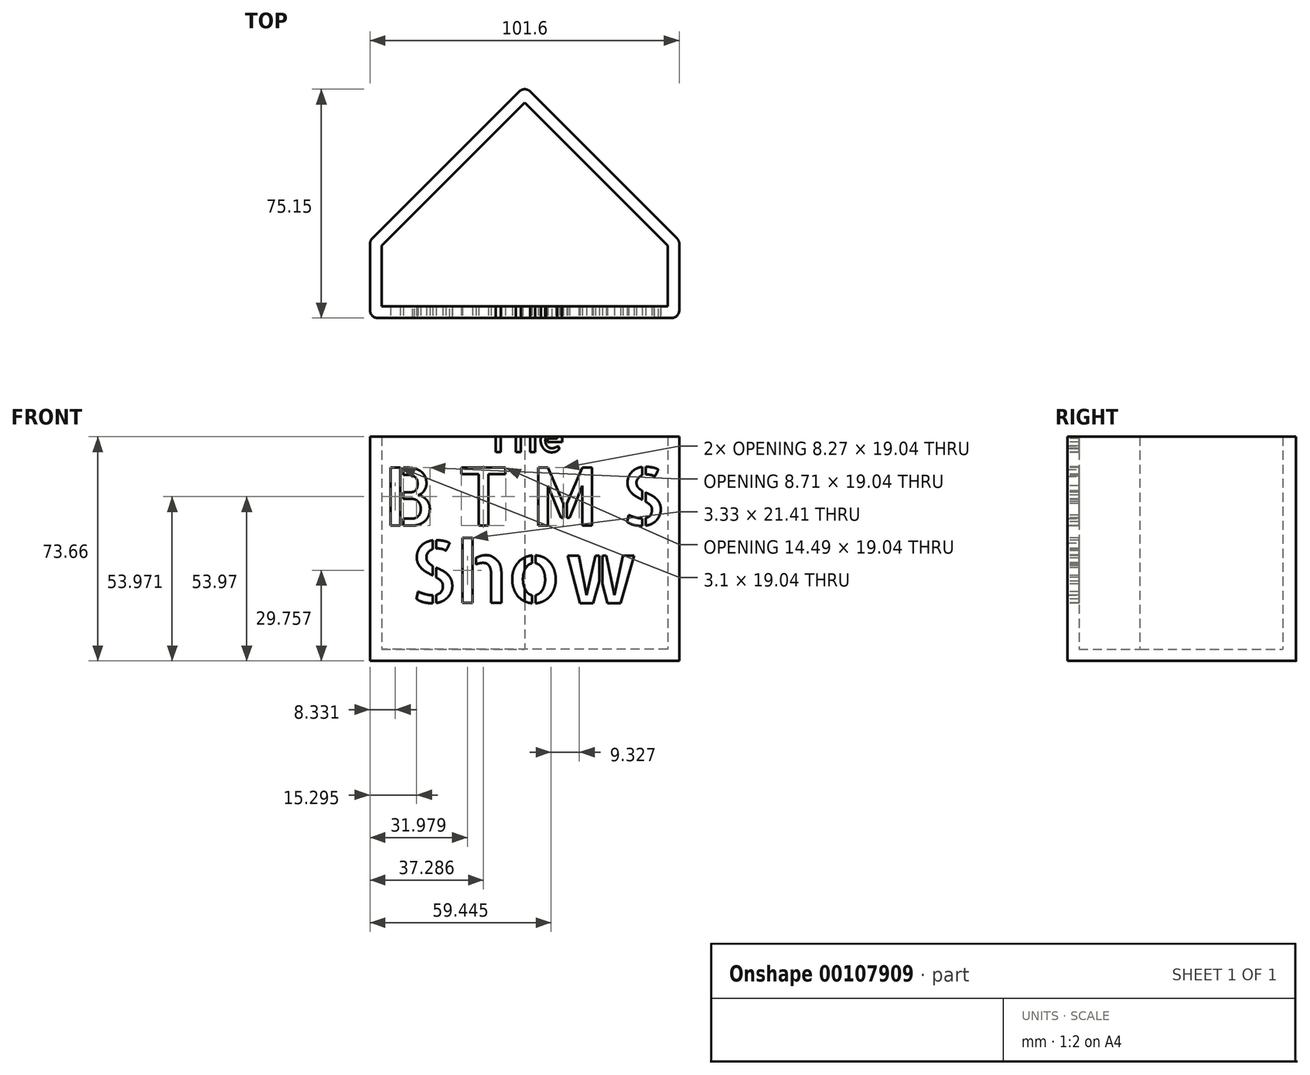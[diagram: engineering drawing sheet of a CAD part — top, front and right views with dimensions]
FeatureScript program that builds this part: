
annotation { "Feature Type Name" : "Feature", "Feature Type Description" : "" }
export const myFeature = defineFeature(function(context is Context, id is Id, definition is map)
    precondition{}
    {
        {
            var Q0;
            Q0=qCreatedBy(makeId("Top.planeOp"),FACE);
            var sketch = newSketch(context, id + "F0", { "sketchPlane" : qUnion([Q0])});
            skLineSegment(sketch, "E0", {"start": v(0, 0) * mm, "end": v(50.8, -76.2) * mm, "construction": true});
            skLineSegment(sketch, "E1", {"start": v(50.8, -76.2) * mm, "end": v(-50.8, -76.2) * mm});
            skLineSegment(sketch, "E2", {"start": v(-50.8, -76.2) * mm, "end": v(0, 0) * mm, "construction": true});
            skLineSegment(sketch, "E3", {"start": v(0, 0) * mm, "end": v(0, -76.2) * mm, "construction": true});
            skLineSegment(sketch, "E4", {"start": v(50.8, -76.2) * mm, "end": v(50.8, -50.8) * mm});
            skLineSegment(sketch, "E5", {"start": v(50.8, -50.8) * mm, "end": v(0, 0) * mm});
            skLineSegment(sketch, "E6", {"start": v(-50.8, -76.2) * mm, "end": v(-50.8, -50.8) * mm});
            skLineSegment(sketch, "E7", {"start": v(-50.8, -50.8) * mm, "end": v(0, 0) * mm});
            skSolve(sketch);
        }
        {
            var Q0;
            Q0=makeQuery(id+"F0.imprint","IMPRINT",FACE,{"disambiguationData":[TD([[makeQuery(id+"F0.imprint","IMPRINT",EDGE,{"derivedFrom":sQuery(id+"F0.wireOp",EDGE,"E1")}),-1.0]])]});
            extrude(context, id + "F1", {"entities" : qUnion([Q0]), "depth" : 3.8 * mm});
        }
        {
            var Q0;
            Q0=makeQuery(id+"F1.opExtrude","CAP_FACE",FACE,{"disambiguationData":[OSD([sQuery(id+"F0.wireOp",EDGE,"E0"),sQuery(id+"F0.wireOp",EDGE,"E1"),sQuery(id+"F0.wireOp",EDGE,"E2")])],"isStart":false});
            var sketch = newSketch(context, id + "F2", { "sketchPlane" : qUnion([Q0])});
            skLineSegment(sketch, "E8.0", {"start": v(-46.99, -52.38) * mm, "end": v(0, -5.39) * mm});
            skLineSegment(sketch, "E8.1", {"start": v(47, -52.38) * mm, "end": v(0, -5.39) * mm});
            skLineSegment(sketch, "E8.2", {"start": v(-46.99, -72.4) * mm, "end": v(-46.99, -52.38) * mm});
            skLineSegment(sketch, "E8.3", {"start": v(47, -72.4) * mm, "end": v(-46.99, -72.4) * mm});
            skLineSegment(sketch, "E8.4", {"start": v(47, -72.4) * mm, "end": v(47, -52.38) * mm});
            skSolve(sketch);
        }
        {
            var Q0;
            Q0=makeQuery(id+"F2.imprint","IMPRINT",FACE,{"disambiguationData":[TD([[makeQuery(id+"F2.imprint","IMPRINT",EDGE,{"derivedFrom":sQuery(id+"F2.wireOp",EDGE,"E8.0")}),1.0]])]});
            extrude(context, id + "F3", {"entities" : qUnion([Q0]), "operationType" : NewBodyOperationType.ADD, "depth" : 69.85 * mm});
        }
        {
            var Q0;
            {var subQ0=sQuery(id+"F0.wireOp",EDGE,"E1");Q0=makeQuery(id+"F3.boolean.opBoolean","MERGE",FACE,{"derivedFrom":[makeQuery(id+"F1.opExtrude","SWEPT_FACE",FACE,{"disambiguationData":[OSD([subQ0])]}),makeQuery(id+"F3.opExtrude","SWEPT_FACE",FACE,{"disambiguationData":[OSD([subQ0])]})]});}
            var sketch = newSketch(context, id + "F4", { "sketchPlane" : qUnion([Q0])});
            skText(sketch, "E9", { "text": "The", "fontName": "AllertaStencil-Regular.ttf"});
            skText(sketch, "E10", { "text": "B T M S", "fontName": "AllertaStencil-Regular.ttf"});
            skText(sketch, "E11", { "text": "Show", "fontName": "AllertaStencil-Regular.ttf"});
            skLineSegment(sketch, "E12", {"start": v(0, 73.66) * mm, "end": v(0, 0) * mm, "construction": true});
            const initialGuessF4  = {"E9": [-0.01326, 0.06858, 1, 0, 0.01016], "E10": [-0.0465, 0.04445, 1, 0, 0.01905], "E11": [-0.0378, 0.01905, 1, 0, 0.02032]};
            skSetInitialGuess(sketch, initialGuessF4);
            skSolve(sketch);
        }
        {
            var Q0;
            Q0=qSketchRegion(id+"F4",true);
            extrude(context, id + "F5", {"entities" : qUnion([Q0]), "operationType" : NewBodyOperationType.REMOVE, "oppositeDirection" : true, "depth" : 5.08 * mm});
        }
        {
            var Q0;
            {var subQ0=sQuery(id+"F0.wireOp",EDGE,"E1");var subQ1=sQuery(id+"F0.wireOp",EDGE,"E0");Q0=makeQuery(id+"F3.boolean.opBoolean","MERGE",EDGE,{"derivedFrom":[makeQuery(id+"F1.opExtrude","SWEPT_EDGE",EDGE,{"disambiguationData":[OSD([subQ1,subQ0])]}),makeQuery(id+"F3.opExtrude","SWEPT_EDGE",EDGE,{"disambiguationData":[OSD([subQ1,subQ0])]})]});}
            var Q1;
            {var subQ0=sQuery(id+"F0.wireOp",EDGE,"E2");var subQ1=sQuery(id+"F0.wireOp",EDGE,"E1");Q1=makeQuery(id+"F3.boolean.opBoolean","MERGE",EDGE,{"derivedFrom":[makeQuery(id+"F1.opExtrude","SWEPT_EDGE",EDGE,{"disambiguationData":[OSD([subQ1,subQ0])]}),makeQuery(id+"F3.opExtrude","SWEPT_EDGE",EDGE,{"disambiguationData":[OSD([subQ1,subQ0])]})]});}
            var Q2;
            {var subQ0=sQuery(id+"F0.wireOp",EDGE,"E5");var subQ1=sQuery(id+"F0.wireOp",EDGE,"E4");Q2=makeQuery(id+"F3.boolean.opBoolean","MERGE",EDGE,{"derivedFrom":[makeQuery(id+"F1.opExtrude","SWEPT_EDGE",EDGE,{"disambiguationData":[OSD([subQ1,subQ0])]}),makeQuery(id+"F3.opExtrude","SWEPT_EDGE",EDGE,{"disambiguationData":[OSD([subQ1,subQ0])]})]});}
            var Q3;
            {var subQ0=sQuery(id+"F0.wireOp",EDGE,"E7");var subQ1=sQuery(id+"F0.wireOp",EDGE,"E5");Q3=makeQuery(id+"F3.boolean.opBoolean","MERGE",EDGE,{"derivedFrom":[makeQuery(id+"F1.opExtrude","SWEPT_EDGE",EDGE,{"disambiguationData":[OSD([subQ1,subQ0])]}),makeQuery(id+"F3.opExtrude","SWEPT_EDGE",EDGE,{"disambiguationData":[OSD([subQ1,subQ0])]})]});}
            var Q4;
            {var subQ0=sQuery(id+"F0.wireOp",EDGE,"E7");var subQ1=sQuery(id+"F0.wireOp",EDGE,"E6");Q4=makeQuery(id+"F3.boolean.opBoolean","MERGE",EDGE,{"derivedFrom":[makeQuery(id+"F1.opExtrude","SWEPT_EDGE",EDGE,{"disambiguationData":[OSD([subQ1,subQ0])]}),makeQuery(id+"F3.opExtrude","SWEPT_EDGE",EDGE,{"disambiguationData":[OSD([subQ1,subQ0])]})]});}
            fillet(context, id + "F6", {"entities" : qUnion([Q0, Q1, Q2, Q3, Q4]), "radius" : 2.54 * mm, "tangentPropagation" : true, "allowEdgeOverflow" : false});
        }
    });
